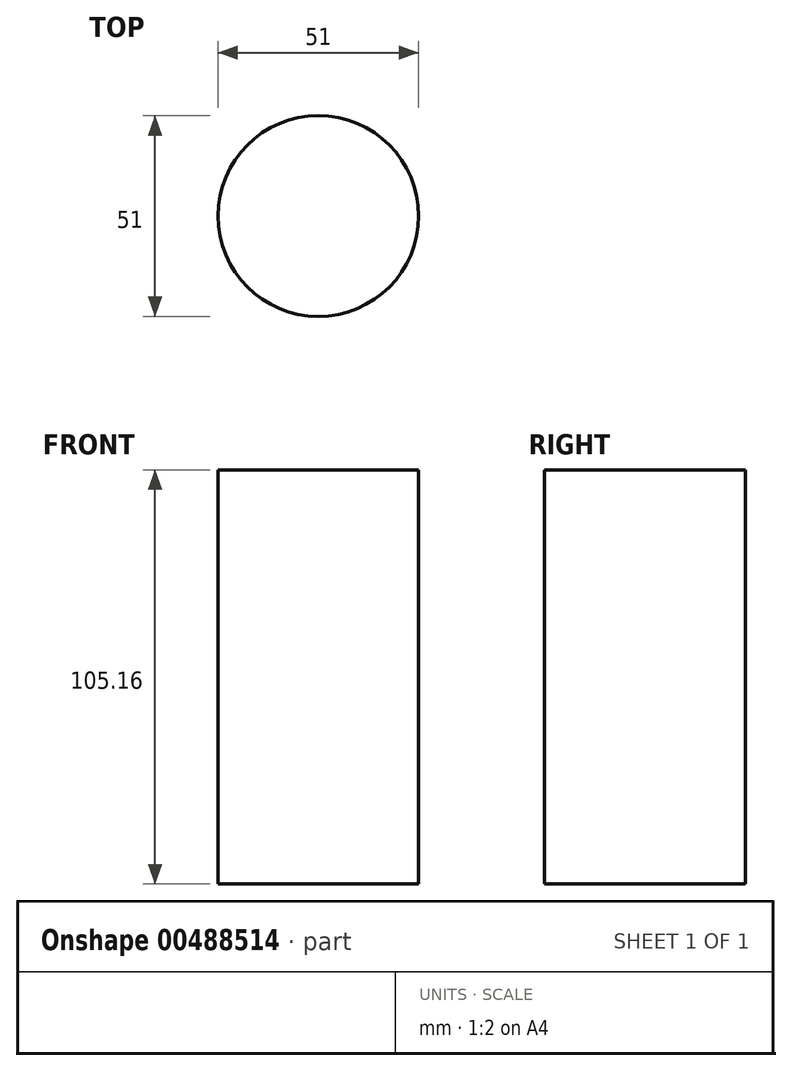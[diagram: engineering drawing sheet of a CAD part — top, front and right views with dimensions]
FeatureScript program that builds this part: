
annotation { "Feature Type Name" : "Feature", "Feature Type Description" : "" }
export const myFeature = defineFeature(function(context is Context, id is Id, definition is map)
    precondition{}
    {
        {
            var Q0;
            Q0=qCreatedBy(makeId("Top.planeOp"),FACE);
            var sketch = newSketch(context, id + "F0", { "sketchPlane" : qUnion([Q0])});
            skCircle(sketch, "E0", {"center": v(0, 0) * mm, "radius": 25.5 * mm});
            skSolve(sketch);
        }
        {
            var Q0;
            Q0 = qSketchRegion(id + "F0", true);
            extrude(context, id + "F1", {"entities" : qUnion([Q0]), "depth" : 105.16 * mm});
        }
        {
            var Q0;
            Q0=qCreatedBy(makeId("Right.planeOp"),FACE);
            var sketch = newSketch(context, id + "F2", { "sketchPlane" : qUnion([Q0])});
            skCircle(sketch, "E1", {"center": v(0, 129.17) * mm, "radius": 35.63 * mm});
            skSolve(sketch);
        }
        {
            var Q0;
            Q0=sQuery(id+"F2.wireOp",EDGE,"E1");
            extrude(context, id + "F3", {"bodyType" : ToolBodyType.SURFACE, "surfaceEntities" : qUnion([Q0]), "endBound" : BoundingType.SYMMETRIC, "depth" : 210.3 * mm});
        }
    });
